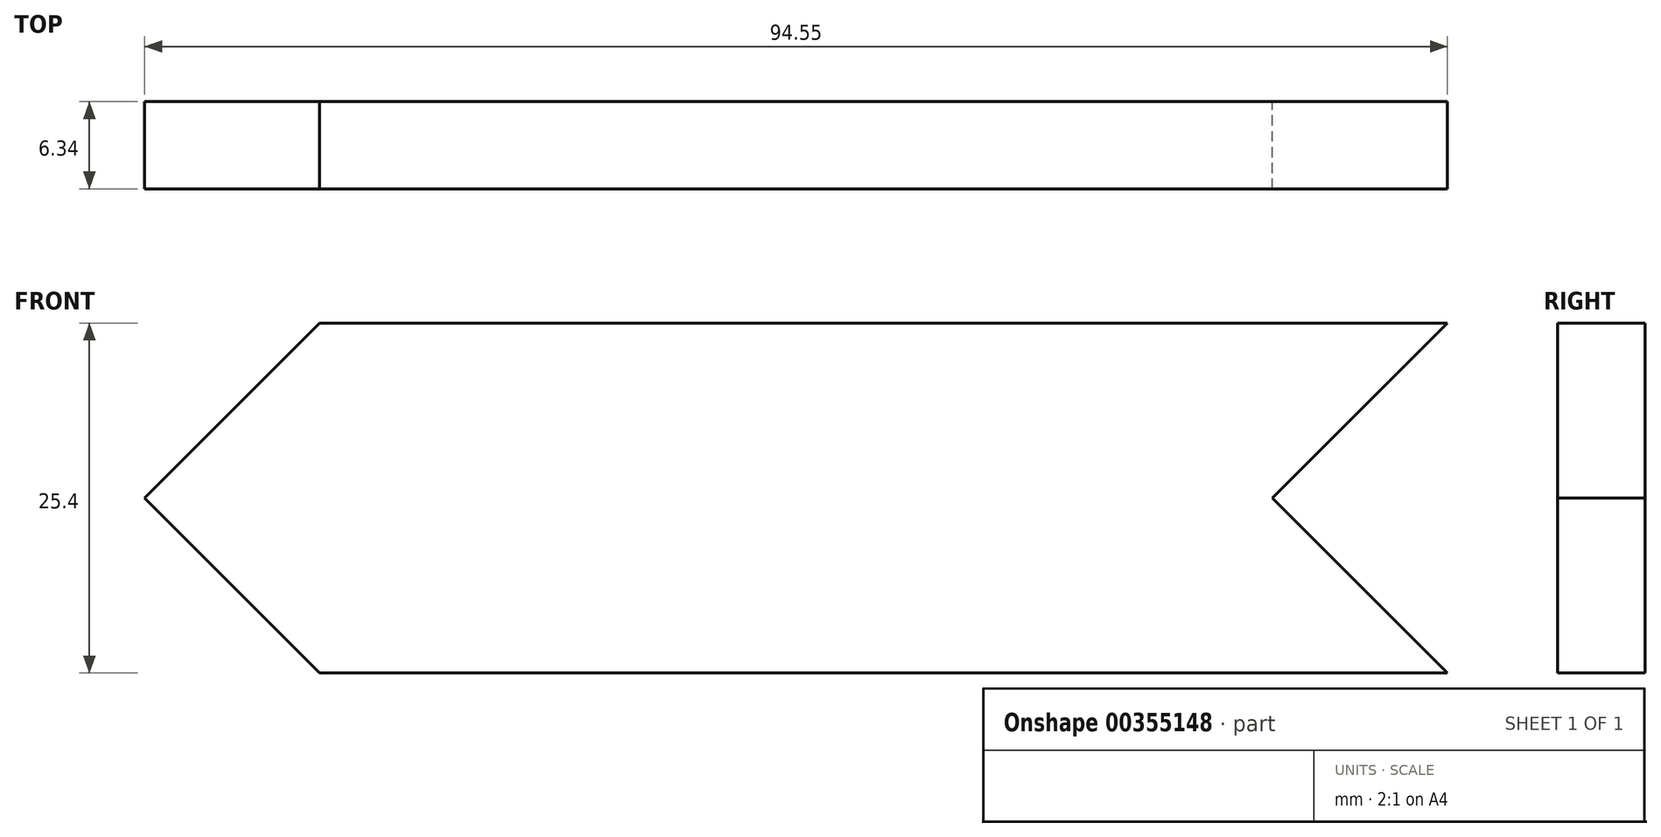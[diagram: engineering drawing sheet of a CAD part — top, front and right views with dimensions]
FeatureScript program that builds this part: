
annotation { "Feature Type Name" : "Feature", "Feature Type Description" : "" }
export const myFeature = defineFeature(function(context is Context, id is Id, definition is map)
    precondition{}
    {
        {
            var Q0;
            Q0=qCreatedBy(makeId("Front.planeOp"),FACE);
            var sketch = newSketch(context, id + "F0", { "sketchPlane" : qUnion([Q0])});
            skLineSegment(sketch, "E0", {"start": v(87.99, -152.4) * mm, "end": v(-263.96, -152.4) * mm});
            skLineSegment(sketch, "E1", {"start": v(-263.96, -152.4) * mm, "end": v(0, 0) * mm});
            skLineSegment(sketch, "E2", {"start": v(0, 0) * mm, "end": v(87.99, -152.4) * mm});
            skLineSegment(sketch, "E3", {"start": v(0, 0) * mm, "end": v(152.4, 87.99) * mm, "construction": true});
            skLineSegment(sketch, "E4", {"start": v(152.4, 87.99) * mm, "end": v(87.99, -152.4) * mm, "construction": true});
            skCircle(sketch, "E5", {"center": v(0, 0) * mm, "radius": 9.53 * mm});
            skCircle(sketch, "E6", {"center": v(0, 0) * mm, "radius": 12.7 * mm});
            skCircle(sketch, "E7", {"center": v(-263.96, -152.4) * mm, "radius": 12.7 * mm});
            skCircle(sketch, "E8", {"center": v(87.99, -152.4) * mm, "radius": 12.7 * mm});
            skLineSegment(sketch, "E9", {"start": v(-6.35, 11) * mm, "end": v(-270.31, -141.4) * mm});
            skLineSegment(sketch, "E10", {"start": v(-263.96, -165.1) * mm, "end": v(87.99, -165.1) * mm});
            skLineSegment(sketch, "E11", {"start": v(98.99, -146.05) * mm, "end": v(11, 6.35) * mm});
            skLineSegment(sketch, "E12", {"start": v(76.99, -158.75) * mm, "end": v(-11, -6.35) * mm});
            skLineSegment(sketch, "E13", {"start": v(-257.61, -163.4) * mm, "end": v(6.35, -11) * mm});
            skLineSegment(sketch, "E14", {"start": v(87.99, -139.7) * mm, "end": v(-263.96, -139.7) * mm});
            skLineSegment(sketch, "E15", {"start": v(87.99, -165.1) * mm, "end": v(109.99, -165.1) * mm});
            skLineSegment(sketch, "E16", {"start": v(98.99, -146.05) * mm, "end": v(109.99, -165.1) * mm});
            skCircle(sketch, "E17", {"center": v(87.99, -152.4) * mm, "radius": 1.59 * mm});
            skCircle(sketch, "E18", {"center": v(-263.96, -152.4) * mm, "radius": 1.59 * mm});
            skLineSegment(sketch, "E19", {"start": v(-270.31, -141.4) * mm, "end": v(-311.36, -165.1) * mm});
            skLineSegment(sketch, "E20", {"start": v(-263.96, -165.1) * mm, "end": v(-311.36, -165.1) * mm});
            skLineSegment(sketch, "E21", {"start": v(-77.11, -139.7) * mm, "end": v(-89.81, -152.4) * mm});
            skLineSegment(sketch, "E22", {"start": v(-89.81, -152.4) * mm, "end": v(-77.11, -165.1) * mm});
            skLineSegment(sketch, "E23", {"start": v(-77.11, -139.7) * mm, "end": v(-77.11, -165.1) * mm});
            skLineSegment(sketch, "E24", {"start": v(-158.96, -139.7) * mm, "end": v(-171.66, -152.4) * mm});
            skLineSegment(sketch, "E25", {"start": v(-171.66, -152.4) * mm, "end": v(-158.96, -165.1) * mm});
            skLineSegment(sketch, "E26", {"start": v(-158.96, -139.7) * mm, "end": v(-158.96, -165.1) * mm});
            skSolve(sketch);
        }
        {
            var Q0;
            {var subQ0=sQuery(id+"F0.wireOp",EDGE,"E21");Q0=makeQuery(id+"F0.imprint","IMPRINT",FACE,{"disambiguationData":[TD([[makeQuery(id+"F0.imprint","IMPRINT",EDGE,{"derivedFrom":subQ0}),-1.0]])]});}
            var Q1;
            {var subQ0=sQuery(id+"F0.wireOp",EDGE,"E22");Q1=makeQuery(id+"F0.imprint","IMPRINT",FACE,{"disambiguationData":[TD([[makeQuery(id+"F0.imprint","IMPRINT",EDGE,{"derivedFrom":subQ0}),-1.0]])]});}
            var Q2;
            {var subQ0=sQuery(id+"F0.wireOp",EDGE,"E24");Q2=makeQuery(id+"F0.imprint","IMPRINT",FACE,{"disambiguationData":[TD([[makeQuery(id+"F0.imprint","IMPRINT",EDGE,{"derivedFrom":subQ0}),1.0]])]});}
            var Q3;
            {var subQ0=sQuery(id+"F0.wireOp",EDGE,"E25");Q3=makeQuery(id+"F0.imprint","IMPRINT",FACE,{"disambiguationData":[TD([[makeQuery(id+"F0.imprint","IMPRINT",EDGE,{"derivedFrom":subQ0}),1.0]])]});}
            extrude(context, id + "F1", {"entities" : qUnion([Q0, Q1, Q2, Q3]), "endBound" : BoundingType.SYMMETRIC, "depth" : 6.35 * mm});
        }
    });
